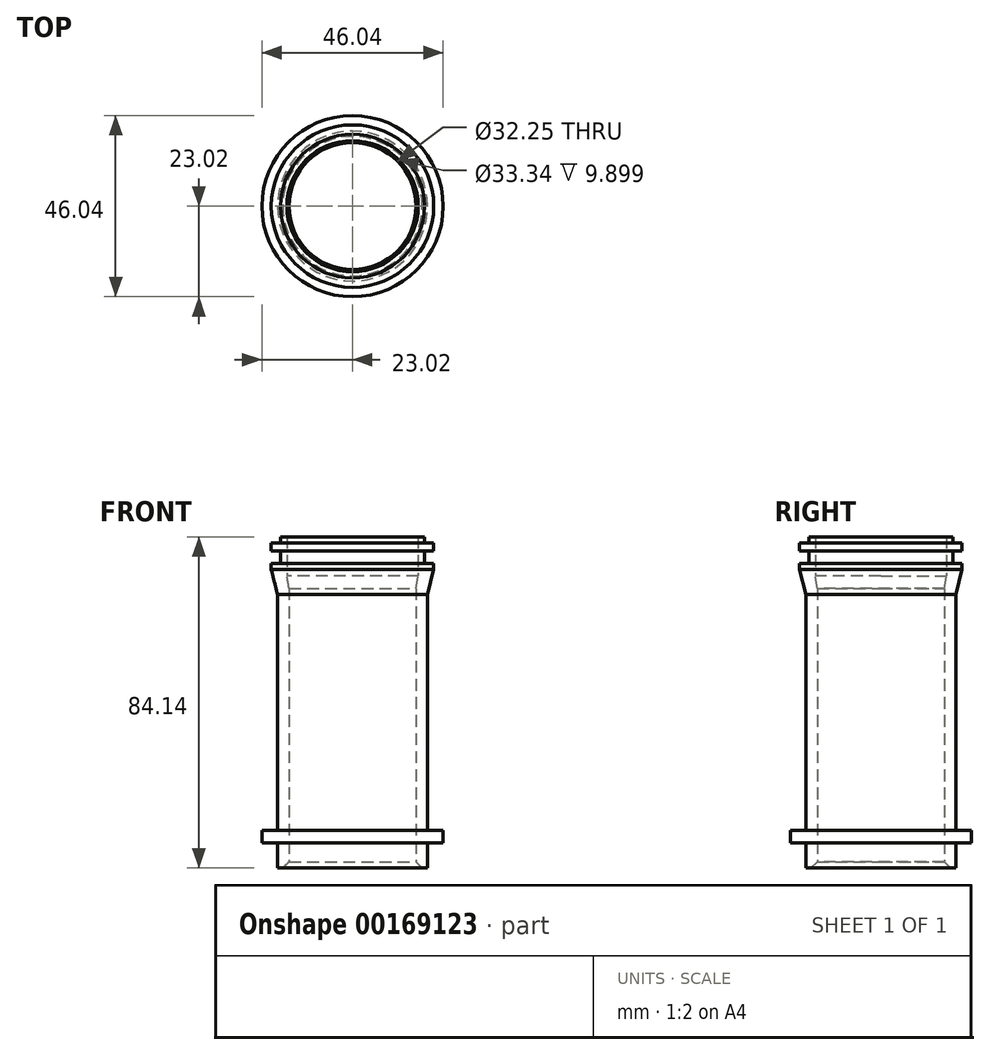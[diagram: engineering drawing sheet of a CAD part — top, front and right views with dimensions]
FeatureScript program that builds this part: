
annotation { "Feature Type Name" : "Feature", "Feature Type Description" : "" }
export const myFeature = defineFeature(function(context is Context, id is Id, definition is map)
    precondition{}
    {
        {
            var Q0;
            Q0=qCreatedBy(makeId("Front.planeOp"),FACE);
            var sketch = newSketch(context, id + "F0", { "sketchPlane" : qUnion([Q0])});
            skLineSegment(sketch, "E0", {"start": v(0, 0) * mm, "end": v(0, 76.2) * mm});
            skLineSegment(sketch, "E1", {"start": v(-16.12, 1.59) * mm, "end": v(-16.12, 75.8) * mm});
            skLineSegment(sketch, "E2", {"start": v(-16.12, 75.8) * mm, "end": v(-16.67, 75.8) * mm});
            skLineSegment(sketch, "E3", {"start": v(-16.67, 75.8) * mm, "end": v(-16.67, 84.14) * mm});
            skLineSegment(sketch, "E4", {"start": v(-16.67, 84.14) * mm, "end": v(-18.26, 84.14) * mm});
            skLineSegment(sketch, "E5", {"start": v(-18.26, 84.14) * mm, "end": v(-18.26, 82.55) * mm});
            skLineSegment(sketch, "E6", {"start": v(-18.26, 82.55) * mm, "end": v(-20.64, 82.55) * mm});
            skLineSegment(sketch, "E7", {"start": v(-20.64, 82.55) * mm, "end": v(-20.64, 80.57) * mm});
            skLineSegment(sketch, "E8", {"start": v(-20.64, 80.57) * mm, "end": v(-18.26, 80.57) * mm});
            skLineSegment(sketch, "E9", {"start": v(-18.26, 80.57) * mm, "end": v(-18.26, 77.4) * mm});
            skLineSegment(sketch, "E10", {"start": v(-18.26, 77.4) * mm, "end": v(-20.64, 77.4) * mm});
            skLineSegment(sketch, "E11", {"start": v(-20.64, 77.4) * mm, "end": v(-20.64, 75.8) * mm});
            skLineSegment(sketch, "E12", {"start": v(-20.64, 75.8) * mm, "end": v(-19.05, 69.45) * mm});
            skLineSegment(sketch, "E13", {"start": v(-19.05, 69.45) * mm, "end": v(-19.05, 9.53) * mm});
            skLineSegment(sketch, "E14", {"start": v(-19.05, 9.53) * mm, "end": v(-23.02, 9.53) * mm});
            skLineSegment(sketch, "E15", {"start": v(-23.02, 9.53) * mm, "end": v(-23.02, 6.35) * mm});
            skLineSegment(sketch, "E16", {"start": v(-23.02, 6.35) * mm, "end": v(-19.05, 6.35) * mm});
            skLineSegment(sketch, "E17", {"start": v(-19.05, 6.35) * mm, "end": v(-19.05, 0) * mm});
            skLineSegment(sketch, "E18", {"start": v(-19.05, 0) * mm, "end": v(-17.71, 0) * mm});
            skLineSegment(sketch, "E19", {"start": v(-16.12, 1.59) * mm, "end": v(-17.71, 0) * mm});
            skSolve(sketch);
        }
        {
            var Q0;
            Q0=makeQuery(id+"F0.imprint","IMPRINT",FACE,{"disambiguationData":[TD([[makeQuery(id+"F0.imprint","IMPRINT",EDGE,{"derivedFrom":sQuery(id+"F0.wireOp",EDGE,"E1")}),1.0]])]});
            var Q1;
            Q1=sQuery(id+"F0.wireOp",EDGE,"E0");
            revolve(context, id + "F1", {"entities" : qUnion([Q0]), "axis" : qUnion([Q1]), "revolveType" : RevolveType.FULL});
        }
        {
            var Q0;
            Q0=makeQuery(id+"F1.opRevolve","SWEPT_EDGE",EDGE,{"disambiguationData":[OSD([sQuery(id+"F0.wireOp",EDGE,"E1"),sQuery(id+"F0.wireOp",EDGE,"E2")])]});
            chamfer(context, id + "F2", {"entities" : qUnion([Q0]), "chamferType" : ChamferType.TWO_OFFSETS, "width1" : 0.81 * mm, "oppositeDirection" : false, "width2" : 4.76 * mm, "tangentPropagation" : true});
        }
    });
